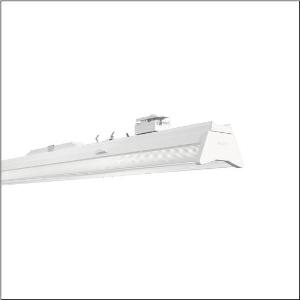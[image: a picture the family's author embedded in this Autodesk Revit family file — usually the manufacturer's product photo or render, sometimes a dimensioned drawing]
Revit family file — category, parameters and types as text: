
# Revit family: licross_21_performance_mo_52td16dn445g
name_source: partatom
category: Lighting Fixtures
units: mm (PartAtom-declared; Revit-internal decimal feet)

## family parameters
Cut with Voids When Loaded = No
Host = Face
Light Source = No
Part Type = Normal
Room Calculation Point = No
Round Connector Dimension = Use Diameter
Shared = No

## types (1)
- --- (1 x LED, 4500 lm, 24.9 W, 4000K)
    Apparent Load = 25 VA
    CIE Flux Codes = 66 88 96 79 100
    Color Rendering = 80
    Color Temperature = 4000K
    Default Elevation = 1800 mm
    Description = Licross 21 Performance MO, luminaire insert, of sheet steel, galvanised, coil coated, white, length: 1.500mm, width: 120mm, height: 123mm, LED rated luminous flux: 4.500lm, light colour: 840, SDCM (Standard Deviation of Colour Matching)MacAdam ≤ 3 SDCM (initial), control gear: DALI 2, with plug, 5-pole, with phase selection, mains connection: 220..240V, AC, 50/60Hz, rated input power: 25W, internal wiring halogen-free, primary light control with lens, of plastic, primary optical cover: cover, of PMMA, CAT 2 (L<= 3000cd/m²), light emission: direct/indirect distribution, primary light characteristic: symmetric, protection rating (complete): IP54, insulation class (complete): insulation class I (protective earthing), certification: CE, ENEC, VDE, UKCA, protection symbol: D if used in an environment with non-conductive dust loads with corresponding accessories, impact resistance: IK06, permissible ambient temperature for indoor applications: -25..+50°C, corresponds to IFS (International Featured Standards) requirements for safety and quality in the food industry, reducing of maximum allowable ambient temperature of 5°C with ceiling mounting, LABS conformity tested according to VDMA 24364:2018-05, The light source and the operating device comply with the requirements of the Ecodesign Regulation (EU) 2019/2020 and are replaceable in accordance with this regulation, packaging unit: 1 piece
    Height = 114 mm
    Lamp = 1 x LED
    Lamp Light Flux = 4500 lm
    Lamp Power = 24.9 W
    Lamp count = 1
    Length = 1500 mm
    Luminous efficacy = 181 lm/W
    Manufacturer = Siteco
    ModVariant = No
    Model = 52TD16DN445G
    Mounting Place = Ceiling
    Mounting Type = Pendant
    Number of Poles = 1
    OnlyDefault = Yes
    Power Factor = 1
    Product Name = Licross 21 Performance MO
    Product group = luminaire insert | ceiling pendant
    ProductGroupID = 901
    Protection Class = Protection class I
    Protection Degree = IP 54
    RLX_Detail_Level = 1
    RLX_Emergency_Light_Flux = 0 lm
    RLX_Emergency_Type = 0
    RLX_Emergency_Type_DB = No
    RlxData = <blob elided: 33849 chars, md5=f28ffdd6>
    Socket = socket
    Standby Power = 0 W
    System Light Flux = 4500 lm
    System Power = 25 W
    Type Comments = factory setting: luminous flux: 100 % | dim-lin: 254 | 165 mA
    Type Image = l_1256138.jpg
    URL = http://relux.com
    VarID = @adj_057787
    Voltage = 0 V
    Weight = 0.00 kg
    Width = 120 mm

## geometry (parser evidence)
native form markers: Blend x4, Sweep x13
no freeform markers — native parametric forms only
